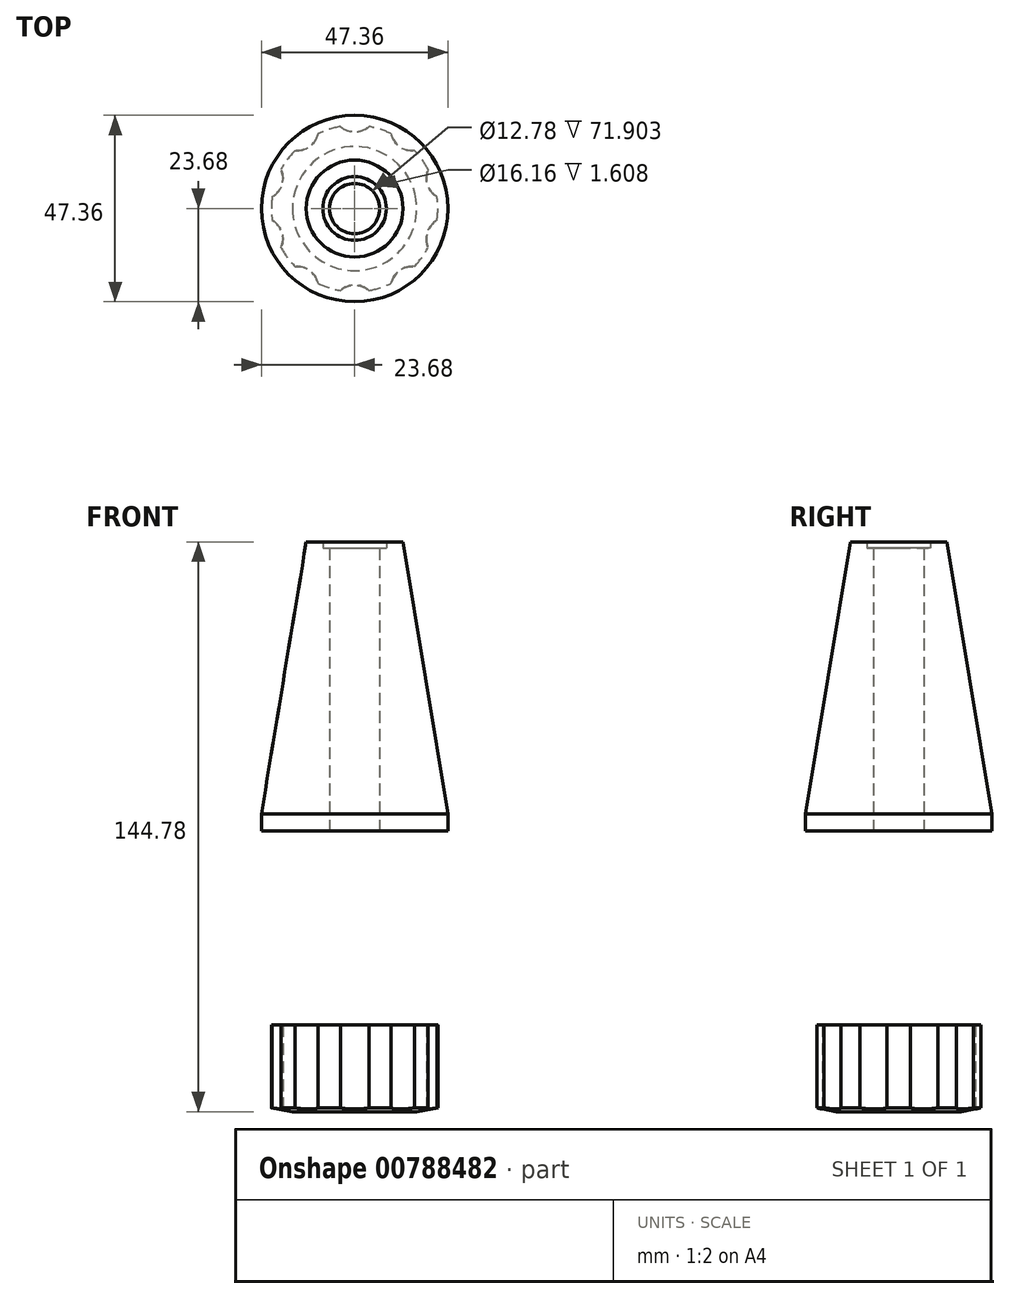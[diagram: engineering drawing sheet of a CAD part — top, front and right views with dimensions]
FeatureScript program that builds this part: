
annotation { "Feature Type Name" : "Feature", "Feature Type Description" : "" }
export const myFeature = defineFeature(function(context is Context, id is Id, definition is map)
    precondition{}
    {
        {
            var Q0;
            Q0=qCreatedBy(makeId("Front.planeOp"),FACE);
            var sketch = newSketch(context, id + "F0", { "sketchPlane" : qUnion([Q0])});
            skLineSegment(sketch, "E0", {"start": v(0, 0) * mm, "end": v(35.87, 0) * mm});
            skLineSegment(sketch, "E1", {"start": v(35.87, 0) * mm, "end": v(35.87, -9.03) * mm});
            skLineSegment(sketch, "E2", {"start": v(35.87, -9.03) * mm, "end": v(30.22, -9.89) * mm});
            skLineSegment(sketch, "E3", {"start": v(30.22, -9.89) * mm, "end": v(30.22, -12.8) * mm});
            skLineSegment(sketch, "E4", {"start": v(30.22, -12.8) * mm, "end": v(35.87, -13.61) * mm});
            skLineSegment(sketch, "E5", {"start": v(35.87, -13.61) * mm, "end": v(35.87, -21.32) * mm});
            skLineSegment(sketch, "E6", {"start": v(35.87, -21.32) * mm, "end": v(21.15, -21.32) * mm});
            skLineSegment(sketch, "E7", {"start": v(21.15, -21.32) * mm, "end": v(21.15, -40.37) * mm});
            skLineSegment(sketch, "E8", {"start": v(21.15, -40.37) * mm, "end": v(18.1, -42.98) * mm});
            skLineSegment(sketch, "E9", {"start": v(18.1, -42.98) * mm, "end": v(18.1, -49.27) * mm});
            skLineSegment(sketch, "E10", {"start": v(18.1, -49.27) * mm, "end": v(21.15, -49.27) * mm});
            skLineSegment(sketch, "E11", {"start": v(21.15, -49.27) * mm, "end": v(21.15, -70.31) * mm});
            skLineSegment(sketch, "E12", {"start": v(15.78, -71.27) * mm, "end": v(21.15, -70.31) * mm});
            skLineSegment(sketch, "E13", {"start": v(15.78, -71.27) * mm, "end": v(0, -71.27) * mm});
            skLineSegment(sketch, "E14", {"start": v(0, -71.27) * mm, "end": v(0, 0) * mm});
            skLineSegment(sketch, "E15", {"start": v(23.68, 0) * mm, "end": v(23.68, 4.42) * mm});
            skLineSegment(sketch, "E16", {"start": v(23.68, 4.42) * mm, "end": v(12.3, 73.51) * mm});
            skLineSegment(sketch, "E17", {"start": v(12.3, 73.51) * mm, "end": v(8.08, 73.51) * mm});
            skLineSegment(sketch, "E18", {"start": v(8.08, 73.51) * mm, "end": v(8.08, 71.9) * mm});
            skLineSegment(sketch, "E19", {"start": v(8.08, 71.9) * mm, "end": v(6.39, 71.9) * mm});
            skLineSegment(sketch, "E20", {"start": v(6.39, 71.9) * mm, "end": v(6.39, 0) * mm});
            skLineSegment(sketch, "E21", {"start": v(18.1, -49.27) * mm, "end": v(0, -49.27) * mm});
            skSolve(sketch);
        }
        {
            var Q0;
            {var subQ0=sQuery(id+"F0.wireOp",EDGE,"E15");Q0=makeQuery(id+"F0.imprint","IMPRINT",FACE,{"disambiguationData":[TD([[makeQuery(id+"F0.imprint","IMPRINT",EDGE,{"derivedFrom":subQ0}),1.0]])]});}
            var Q1;
            {var subQ6=sQuery(id+"F0.wireOp",EDGE,"E1");Q1=makeQuery(id+"F0.imprint","IMPRINT",FACE,{"disambiguationData":[TD([[makeQuery(id+"F0.imprint","IMPRINT",EDGE,{"derivedFrom":subQ6}),-1.0]])]});}
            var Q2;
            Q2=sQuery(id+"F0.wireOp",EDGE,"E14");
            revolve(context, id + "F1", {"entities" : qUnion([Q0, Q1]), "axis" : qUnion([Q2]), "revolveType" : RevolveType.FULL});
        }
        {
            var Q0;
            Q0=makeQuery(id+"F0.imprint","IMPRINT",FACE,{"disambiguationData":[TD([[makeQuery(id+"F0.imprint","IMPRINT",EDGE,{"derivedFrom":sQuery(id+"F0.wireOp",EDGE,"E10")}),-1.0]])]});
            var Q1;
            Q1=sQuery(id+"F0.wireOp",EDGE,"E14");
            revolve(context, id + "F2", {"entities" : qUnion([Q0]), "axis" : qUnion([Q1]), "revolveType" : RevolveType.FULL});
        }
        {
            var Q0;
            Q0=makeQuery(id+"F2.opRevolve","SWEPT_FACE",FACE,{"disambiguationData":[OSD([sQuery(id+"F0.wireOp",EDGE,"E13")])]});
            var sketch = newSketch(context, id + "F3", { "sketchPlane" : qUnion([Q0])});
            skCircle(sketch, "E22", {"center": v(0, 24.9) * mm, "radius": 5.46 * mm});
            skCircle(sketch, "E23.1.0", {"center": v(-14.64, 20.15) * mm, "radius": 5.46 * mm});
            skCircle(sketch, "E23.2.0", {"center": v(-23.69, 7.7) * mm, "radius": 5.46 * mm});
            skCircle(sketch, "E23.3.0", {"center": v(-23.69, -7.7) * mm, "radius": 5.46 * mm});
            skCircle(sketch, "E23.4.0", {"center": v(-14.64, -20.15) * mm, "radius": 5.46 * mm});
            skCircle(sketch, "E23.5.0", {"center": v(0, -24.9) * mm, "radius": 5.46 * mm});
            skCircle(sketch, "E23.6.0", {"center": v(14.64, -20.15) * mm, "radius": 5.46 * mm});
            skCircle(sketch, "E23.7.0", {"center": v(23.69, -7.7) * mm, "radius": 5.46 * mm});
            skCircle(sketch, "E23.8.0", {"center": v(23.69, 7.7) * mm, "radius": 5.46 * mm});
            skCircle(sketch, "E23.9.0", {"center": v(14.64, 20.15) * mm, "radius": 5.46 * mm});
            skPoint(sketch, "E23.center", {"position": v(0, 0) * mm});
            skSolve(sketch);
        }
        {
            var Q0;
            Q0=qSketchRegion(id+"F3",true);
            extrude(context, id + "F4", {"entities" : qUnion([Q0]), "operationType" : NewBodyOperationType.REMOVE, "oppositeDirection" : true, "depth" : 25.4 * mm, "offsetDistance" : 25.4 * mm});
        }
    });
